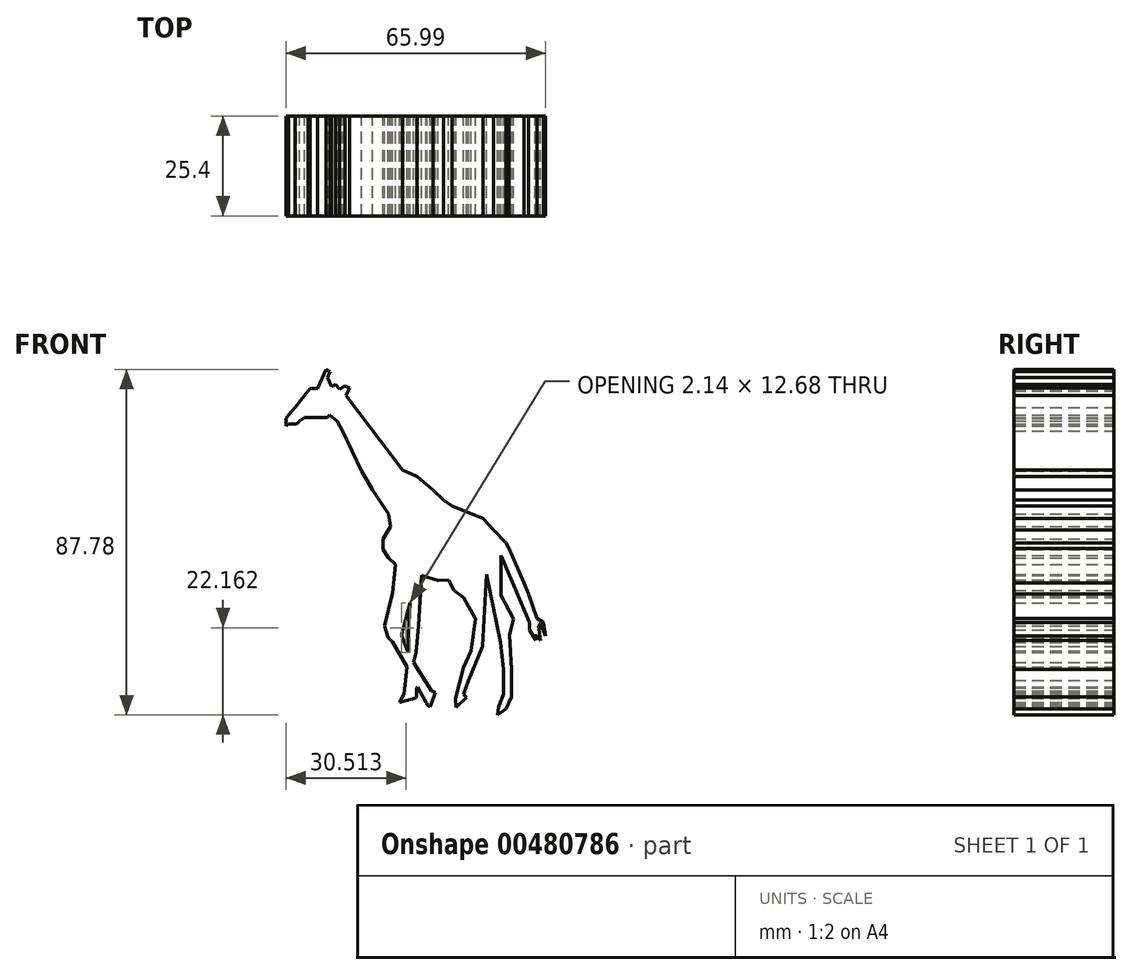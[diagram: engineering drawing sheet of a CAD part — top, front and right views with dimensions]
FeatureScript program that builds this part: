
annotation { "Feature Type Name" : "Feature", "Feature Type Description" : "" }
export const myFeature = defineFeature(function(context is Context, id is Id, definition is map)
    precondition{}
    {
        {
            var Q0;
            Q0=qCreatedBy(makeId("Front.planeOp"),FACE);
            var sketch = newSketch(context, id + "F0", { "sketchPlane" : qUnion([Q0])});
            skLineSegment(sketch, "E0", {"start": v(-18.8, 20) * mm, "end": v(-4.8, 1.58) * mm});
            skLineSegment(sketch, "E1", {"start": v(-4.8, 1.58) * mm, "end": v(-1.12, 0) * mm});
            skLineSegment(sketch, "E2", {"start": v(-1.12, 0) * mm, "end": v(2.93, -3.46) * mm});
            skLineSegment(sketch, "E3", {"start": v(2.93, -3.46) * mm, "end": v(5.5, -6.04) * mm});
            skLineSegment(sketch, "E4", {"start": v(5.5, -6.04) * mm, "end": v(7.72, -7.5) * mm});
            skLineSegment(sketch, "E5", {"start": v(7.72, -7.5) * mm, "end": v(15.58, -10.7) * mm});
            skLineSegment(sketch, "E6", {"start": v(15.58, -10.7) * mm, "end": v(18.28, -13.65) * mm});
            skLineSegment(sketch, "E7", {"start": v(20.12, -17.09) * mm, "end": v(20.12, -27.65) * mm});
            skLineSegment(sketch, "E8", {"start": v(18.28, -13.65) * mm, "end": v(21.47, -16.96) * mm});
            skLineSegment(sketch, "E9", {"start": v(21.47, -16.96) * mm, "end": v(22.2, -18.31) * mm});
            skLineSegment(sketch, "E10", {"start": v(20.12, -27.65) * mm, "end": v(20.12, -30.2) * mm});
            skLineSegment(sketch, "E11", {"start": v(20.12, -30.2) * mm, "end": v(23.37, -36.27) * mm});
            skLineSegment(sketch, "E12", {"start": v(23.37, -36.27) * mm, "end": v(22.34, -40.29) * mm});
            skLineSegment(sketch, "E13", {"start": v(22.34, -40.29) * mm, "end": v(22.77, -49.07) * mm});
            skLineSegment(sketch, "E14", {"start": v(22.77, -49.07) * mm, "end": v(22.77, -56) * mm});
            skLineSegment(sketch, "E15", {"start": v(22.77, -56) * mm, "end": v(21.47, -59.01) * mm});
            skLineSegment(sketch, "E16", {"start": v(21.47, -59.01) * mm, "end": v(19.24, -60.6) * mm});
            skLineSegment(sketch, "E17", {"start": v(19.24, -60.6) * mm, "end": v(19.6, -58.64) * mm});
            skLineSegment(sketch, "E18", {"start": v(19.6, -58.64) * mm, "end": v(20.8, -55.27) * mm});
            skLineSegment(sketch, "E19", {"start": v(20.8, -55.27) * mm, "end": v(20.8, -52.51) * mm});
            skLineSegment(sketch, "E20", {"start": v(20.8, -52.51) * mm, "end": v(20.8, -49.07) * mm});
            skLineSegment(sketch, "E21", {"start": v(20.8, -49.07) * mm, "end": v(20.06, -42.19) * mm});
            skLineSegment(sketch, "E22", {"start": v(11.87, -51.88) * mm, "end": v(10.7, -55.37) * mm});
            skLineSegment(sketch, "E23", {"start": v(10.7, -55.37) * mm, "end": v(11.4, -56.1) * mm});
            skLineSegment(sketch, "E24", {"start": v(11.4, -56.1) * mm, "end": v(8.72, -58.66) * mm});
            skLineSegment(sketch, "E25", {"start": v(8.72, -58.66) * mm, "end": v(8.6, -56.42) * mm});
            skLineSegment(sketch, "E26", {"start": v(8.6, -56.42) * mm, "end": v(10.7, -48.53) * mm});
            skLineSegment(sketch, "E27", {"start": v(10.7, -48.53) * mm, "end": v(12.5, -44.31) * mm});
            skLineSegment(sketch, "E28", {"start": v(12.5, -44.31) * mm, "end": v(13.63, -36.27) * mm});
            skLineSegment(sketch, "E29", {"start": v(13.63, -36.27) * mm, "end": v(10.7, -30.8) * mm});
            skLineSegment(sketch, "E30", {"start": v(10.7, -30.8) * mm, "end": v(8.26, -29.03) * mm});
            skLineSegment(sketch, "E31", {"start": v(8.26, -29.03) * mm, "end": v(6.78, -26.26) * mm});
            skLineSegment(sketch, "E32", {"start": v(6.78, -26.26) * mm, "end": v(4.17, -26.39) * mm});
            skLineSegment(sketch, "E33", {"start": v(4.17, -26.39) * mm, "end": v(0, -25.21) * mm});
            skLineSegment(sketch, "E34", {"start": v(0, -25.21) * mm, "end": v(-0.74, -37.98) * mm});
            skLineSegment(sketch, "E35", {"start": v(-0.74, -37.98) * mm, "end": v(-1.46, -44.78) * mm});
            skLineSegment(sketch, "E36", {"start": v(-1.46, -44.78) * mm, "end": v(-2.07, -47.25) * mm});
            skLineSegment(sketch, "E37", {"start": v(-2.07, -47.25) * mm, "end": v(2.5, -54.47) * mm});
            skLineSegment(sketch, "E38", {"start": v(-3.76, -48.4) * mm, "end": v(-7.4, -42.1) * mm});
            skLineSegment(sketch, "E39", {"start": v(-7.4, -42.1) * mm, "end": v(-8.54, -40.96) * mm});
            skLineSegment(sketch, "E40", {"start": v(-8.54, -40.96) * mm, "end": v(-9.39, -37.98) * mm});
            skLineSegment(sketch, "E41", {"start": v(-9.39, -37.98) * mm, "end": v(-7.4, -29.54) * mm});
            skLineSegment(sketch, "E42", {"start": v(-7.4, -29.54) * mm, "end": v(-6.65, -22.42) * mm});
            skLineSegment(sketch, "E43", {"start": v(-6.65, -22.42) * mm, "end": v(0, -25.21) * mm});
            skLineSegment(sketch, "E44", {"start": v(-3.5, -44.78) * mm, "end": v(-3.5, -41.38) * mm});
            skPoint(sketch, "E44.endSnap0", {"position": v(-1.1, -41.38) * mm});
            skLineSegment(sketch, "E45", {"start": v(-3.5, -41.38) * mm, "end": v(-3.37, -40.26) * mm});
            skLineSegment(sketch, "E46", {"start": v(-3.37, -40.26) * mm, "end": v(-2.9, -32.1) * mm});
            skLineSegment(sketch, "E47", {"start": v(-2.07, -47.25) * mm, "end": v(-3.5, -44.78) * mm});
            skLineSegment(sketch, "E48", {"start": v(-3.76, -48.4) * mm, "end": v(-4.48, -55.21) * mm});
            skLineSegment(sketch, "E49", {"start": v(0, -52.43) * mm, "end": v(-1.35, -53.77) * mm});
            skLineSegment(sketch, "E50", {"start": v(-1.35, -53.77) * mm, "end": v(-1.35, -55.8) * mm});
            skLineSegment(sketch, "E51", {"start": v(-1.35, -55.8) * mm, "end": v(-1.4, -56.25) * mm});
            skLineSegment(sketch, "E52", {"start": v(-1.4, -56.25) * mm, "end": v(-5.6, -57.39) * mm});
            skLineSegment(sketch, "E53", {"start": v(-5.6, -57.39) * mm, "end": v(-4.48, -55.21) * mm});
            skLineSegment(sketch, "E54", {"start": v(-3.5, -44.78) * mm, "end": v(-5.04, -40.26) * mm});
            skLineSegment(sketch, "E55", {"start": v(-5.04, -40.26) * mm, "end": v(-2.9, -32.1) * mm});
            skLineSegment(sketch, "E56", {"start": v(-2.9, -32.1) * mm, "end": v(0, -25.21) * mm});
            skLineSegment(sketch, "E57", {"start": v(-6.65, -22.42) * mm, "end": v(-8.38, -20.67) * mm});
            skLineSegment(sketch, "E58", {"start": v(-8.38, -20.67) * mm, "end": v(-9.81, -18.56) * mm});
            skLineSegment(sketch, "E59", {"start": v(-9.81, -18.56) * mm, "end": v(-9.81, -15.93) * mm});
            skLineSegment(sketch, "E60", {"start": v(-9.81, -15.93) * mm, "end": v(-7.9, -12.75) * mm});
            skLineSegment(sketch, "E61", {"start": v(-7.9, -12.75) * mm, "end": v(-8.43, -9.52) * mm});
            skLineSegment(sketch, "E62", {"start": v(-8.43, -9.52) * mm, "end": v(-12.45, -3.47) * mm});
            skLineSegment(sketch, "E63", {"start": v(-12.45, -3.47) * mm, "end": v(-15.26, 1.33) * mm});
            skLineSegment(sketch, "E64", {"start": v(-15.26, 1.33) * mm, "end": v(-20.13, 11.5) * mm});
            skLineSegment(sketch, "E65", {"start": v(-20.13, 11.5) * mm, "end": v(-21.48, 14.1) * mm});
            skLineSegment(sketch, "E66", {"start": v(-21.48, 14.1) * mm, "end": v(-23.4, 15.6) * mm});
            skLineSegment(sketch, "E67", {"start": v(-23.4, 15.6) * mm, "end": v(-23.92, 14.94) * mm});
            skLineSegment(sketch, "E68", {"start": v(-23.92, 14.94) * mm, "end": v(-26.48, 14.94) * mm});
            skLineSegment(sketch, "E69", {"start": v(-26.48, 14.94) * mm, "end": v(-29.73, 14.94) * mm});
            skLineSegment(sketch, "E70", {"start": v(-29.73, 14.94) * mm, "end": v(-30.99, 14.03) * mm});
            skLineSegment(sketch, "E71", {"start": v(-30.99, 14.03) * mm, "end": v(-31.77, 13.37) * mm});
            skLineSegment(sketch, "E72", {"start": v(-31.77, 13.37) * mm, "end": v(-33.82, 13.37) * mm});
            skLineSegment(sketch, "E73", {"start": v(-33.82, 13.37) * mm, "end": v(-34.48, 12.77) * mm});
            skLineSegment(sketch, "E74", {"start": v(-34.48, 12.77) * mm, "end": v(-34.48, 14.76) * mm});
            skLineSegment(sketch, "E75", {"start": v(-34.48, 14.76) * mm, "end": v(-33.82, 15.6) * mm});
            skLineSegment(sketch, "E76", {"start": v(-33.82, 15.6) * mm, "end": v(-32.13, 17.46) * mm});
            skLineSegment(sketch, "E77", {"start": v(-32.13, 17.46) * mm, "end": v(-28.88, 21.68) * mm});
            skLineSegment(sketch, "E78", {"start": v(-28.88, 21.68) * mm, "end": v(-28.28, 22.37) * mm});
            skLineSegment(sketch, "E79", {"start": v(-28.28, 22.37) * mm, "end": v(-26.42, 22.37) * mm});
            skLineSegment(sketch, "E80", {"start": v(-26.42, 22.37) * mm, "end": v(-24.33, 27.18) * mm});
            skLineSegment(sketch, "E81", {"start": v(-24.33, 27.18) * mm, "end": v(-23.22, 26.7) * mm});
            skLineSegment(sketch, "E82", {"start": v(-23.22, 26.7) * mm, "end": v(-23.92, 25.08) * mm});
            skLineSegment(sketch, "E83", {"start": v(-23.92, 25.08) * mm, "end": v(-22.85, 22.84) * mm});
            skLineSegment(sketch, "E84", {"start": v(-22.85, 22.84) * mm, "end": v(-21.89, 23.3) * mm});
            skLineSegment(sketch, "E85", {"start": v(-21.89, 23.3) * mm, "end": v(-20.85, 22.23) * mm});
            skLineSegment(sketch, "E86", {"start": v(-20.85, 22.23) * mm, "end": v(-19.47, 22.94) * mm});
            skLineSegment(sketch, "E87", {"start": v(-19.47, 22.94) * mm, "end": v(-18.33, 22.42) * mm});
            skLineSegment(sketch, "E88", {"start": v(-18.33, 22.42) * mm, "end": v(-19.2, 20.51) * mm});
            skLineSegment(sketch, "E89", {"start": v(-19.2, 20.51) * mm, "end": v(-18.8, 20) * mm});
            skLineSegment(sketch, "E90", {"start": v(-3.76, -48.4) * mm, "end": v(1.08, -57.42) * mm});
            skLineSegment(sketch, "E91", {"start": v(2.5, -54.47) * mm, "end": v(3.55, -54.88) * mm});
            skLineSegment(sketch, "E92", {"start": v(3.55, -54.88) * mm, "end": v(2.1, -58.54) * mm});
            skLineSegment(sketch, "E93", {"start": v(2.1, -58.54) * mm, "end": v(1.35, -58.04) * mm});
            skLineSegment(sketch, "E94", {"start": v(1.35, -58.04) * mm, "end": v(1.35, -57.42) * mm});
            skLineSegment(sketch, "E95", {"start": v(1.35, -57.54) * mm, "end": v(1.08, -57.42) * mm});
            skLineSegment(sketch, "E96", {"start": v(15.41, -43.2) * mm, "end": v(11.87, -51.88) * mm});
            skLineSegment(sketch, "E97", {"start": v(15.41, -43.2) * mm, "end": v(16.53, -24.94) * mm});
            skLineSegment(sketch, "E98", {"start": v(16.53, -24.94) * mm, "end": v(20.06, -42.19) * mm});
            skLineSegment(sketch, "E99", {"start": v(22.2, -18.31) * mm, "end": v(26.01, -27.06) * mm});
            skLineSegment(sketch, "E100", {"start": v(26.01, -27.06) * mm, "end": v(27.11, -29.9) * mm});
            skLineSegment(sketch, "E101", {"start": v(27.11, -29.9) * mm, "end": v(29.28, -36.02) * mm});
            skLineSegment(sketch, "E102", {"start": v(29.28, -36.02) * mm, "end": v(31.01, -37.08) * mm});
            skLineSegment(sketch, "E103", {"start": v(27.47, -39.04) * mm, "end": v(27.47, -37.08) * mm});
            skLineSegment(sketch, "E104", {"start": v(27.47, -37.08) * mm, "end": v(20.12, -20.13) * mm});
            skLineSegment(sketch, "E105", {"start": v(31.01, -37.08) * mm, "end": v(31.51, -40.5) * mm});
            skLineSegment(sketch, "E106", {"start": v(31.51, -40.5) * mm, "end": v(30.25, -37.4) * mm});
            skLineSegment(sketch, "E107", {"start": v(30.25, -37.4) * mm, "end": v(29.67, -37.97) * mm});
            skLineSegment(sketch, "E108", {"start": v(29.67, -37.97) * mm, "end": v(30.22, -41.68) * mm});
            skLineSegment(sketch, "E109", {"start": v(30.22, -41.68) * mm, "end": v(29.34, -40.5) * mm});
            skLineSegment(sketch, "E110", {"start": v(29.34, -40.5) * mm, "end": v(28.83, -40.57) * mm});
            skLineSegment(sketch, "E111", {"start": v(28.83, -40.57) * mm, "end": v(29, -41.68) * mm});
            skLineSegment(sketch, "E112", {"start": v(29, -41.68) * mm, "end": v(27.47, -39.04) * mm});
            skSolve(sketch);
        }
        {
            var Q0;
            Q0=makeQuery(id+"F0.imprint","IMPRINT",FACE,{"disambiguationData":[TD([[makeQuery(id+"F0.imprint","IMPRINT",EDGE,{"derivedFrom":sQuery(id+"F0.wireOp",EDGE,"E0")}),-1.0]])]});
            var Q1;
            Q1=makeQuery(id+"F0.imprint","IMPRINT",FACE,{"disambiguationData":[TD([[makeQuery(id+"F0.imprint","IMPRINT",EDGE,{"derivedFrom":sQuery(id+"F0.wireOp",EDGE,"E37")}),-1.0]])]});
            var Q2;
            Q2=makeQuery(id+"F0.imprint","IMPRINT",FACE,{"disambiguationData":[TD([[makeQuery(id+"F0.imprint","IMPRINT",EDGE,{"derivedFrom":sQuery(id+"F0.wireOp",EDGE,"E34")}),-1.0]])]});
            var Q3;
            {var subQ1=sQuery(id+"F0.wireOp",EDGE,"E48");Q3=makeQuery(id+"F0.imprint","IMPRINT",FACE,{"disambiguationData":[TD([[makeQuery(id+"F0.imprint","IMPRINT",EDGE,{"derivedFrom":subQ1}),1.0]])]});}
            extrude(context, id + "F1", {"entities" : qUnion([Q0, Q1, Q2, Q3]), "depth" : 25.4 * mm});
        }
    });
